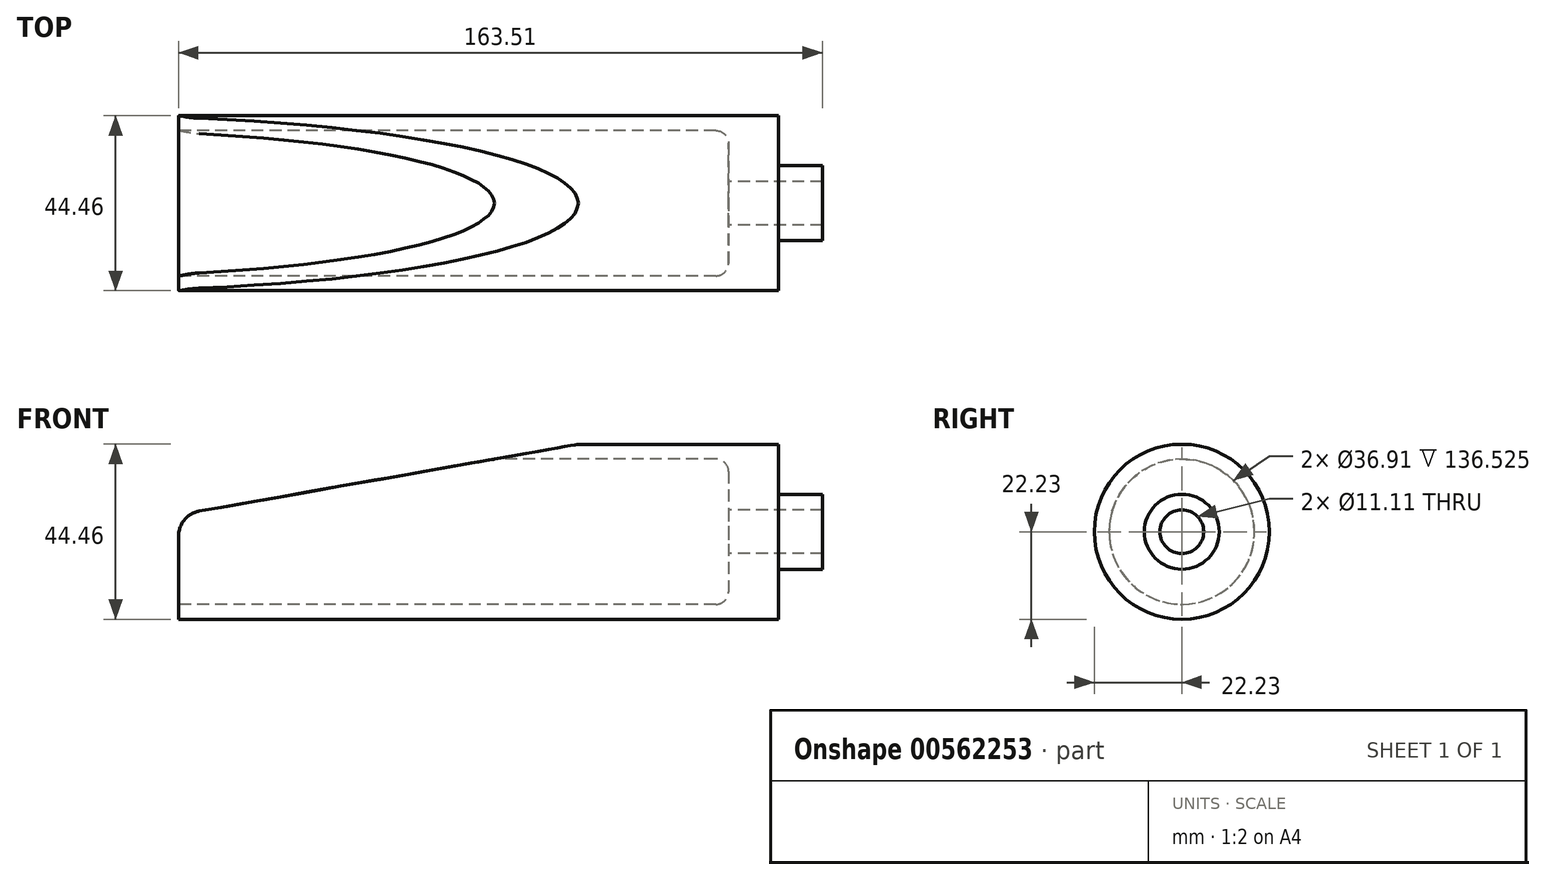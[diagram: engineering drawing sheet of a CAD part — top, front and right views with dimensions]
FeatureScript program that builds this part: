
annotation { "Feature Type Name" : "Feature", "Feature Type Description" : "" }
export const myFeature = defineFeature(function(context is Context, id is Id, definition is map)
    precondition{}
    {
        {
            var Q0;
            Q0=qCreatedBy(makeId("Front.planeOp"),FACE);
            var sketch = newSketch(context, id + "F0", { "sketchPlane" : qUnion([Q0])});
            skLineSegment(sketch, "E0", {"start": v(-163.51, 0) * mm, "end": v(0, 0) * mm, "construction": true});
            skLineSegment(sketch, "E1", {"start": v(0, 0) * mm, "end": v(0, 0) * mm});
            skLineSegment(sketch, "E2", {"start": v(0, -9.53) * mm, "end": v(-11.11, -9.53) * mm});
            skLineSegment(sketch, "E3", {"start": v(-11.11, -9.53) * mm, "end": v(-11.11, -22.23) * mm});
            skLineSegment(sketch, "E4", {"start": v(-11.11, -22.23) * mm, "end": v(-163.51, -22.23) * mm});
            skLineSegment(sketch, "E5", {"start": v(-163.51, -22.23) * mm, "end": v(-163.51, -18.46) * mm});
            skLineSegment(sketch, "E6", {"start": v(-163.51, -18.46) * mm, "end": v(-26.99, -18.46) * mm});
            skLineSegment(sketch, "E7", {"start": v(-23.81, -15.28) * mm, "end": v(-23.81, -5.56) * mm});
            skLineSegment(sketch, "E8", {"start": v(-23.81, 0) * mm, "end": v(0, 0) * mm, "construction": true});
            skLineSegment(sketch, "E9", {"start": v(0, 0) * mm, "end": v(0, -5.56) * mm, "construction": true});
            skPoint(sketch, "E10.visualSharp", {"position": v(-23.81, -18.46) * mm});
            skArc(sketch, "E10.filletArc", {"start": v(-26.99, -18.46) * mm, "mid": v(-24.74, -17.53) * mm, "end": v(-23.81, -15.28) * mm});
            skLineSegment(sketch, "E11", {"start": v(-23.81, -5.56) * mm, "end": v(0, -5.56) * mm});
            skLineSegment(sketch, "E12", {"start": v(-23.81, -5.56) * mm, "end": v(-23.81, 0) * mm, "construction": true});
            skLineSegment(sketch, "E13", {"start": v(0, -5.56) * mm, "end": v(0, -5.56) * mm});
            skLineSegment(sketch, "E14", {"start": v(0, -5.56) * mm, "end": v(0, -9.53) * mm});
            skSolve(sketch);
        }
        {
            var Q0;
            Q0=qSketchRegion(id+"F0",true);
            var Q1;
            Q1=sQuery(id+"F0.wireOp",EDGE,"E0");
            revolve(context, id + "F1", {"entities" : qUnion([Q0]), "axis" : qUnion([Q1]), "revolveType" : RevolveType.FULL});
        }
        {
            var Q0;
            Q0=qCreatedBy(makeId("Front.planeOp"),FACE);
            var sketch = newSketch(context, id + "F2", { "sketchPlane" : qUnion([Q0])});
            skLineSegment(sketch, "E15", {"start": v(-169.86, 22.22) * mm, "end": v(-61.91, 22.22) * mm});
            skLineSegment(sketch, "E16", {"start": v(-61.91, 22.22) * mm, "end": v(-158.27, 5.24) * mm});
            skLineSegment(sketch, "E17", {"start": v(-163.51, -1.02) * mm, "end": v(-163.51, -22.22) * mm});
            skLineSegment(sketch, "E18", {"start": v(-163.51, -22.22) * mm, "end": v(-169.86, -22.22) * mm});
            skLineSegment(sketch, "E19", {"start": v(-169.86, -22.22) * mm, "end": v(-169.86, 22.22) * mm});
            skPoint(sketch, "E20.visualSharp", {"position": v(-163.51, 4.31) * mm});
            skArc(sketch, "E20.filletArc", {"start": v(-158.27, 5.24) * mm, "mid": v(-162.03, 3.06) * mm, "end": v(-163.51, -1.02) * mm});
            skLineSegment(sketch, "E21", {"start": v(-169.86, 0) * mm, "end": v(0, 0) * mm, "construction": true});
            skSolve(sketch);
        }
        {
            var Q0;
            Q0=qSketchRegion(id+"F2",true);
            extrude(context, id + "F3", {"entities" : qUnion([Q0]), "operationType" : NewBodyOperationType.REMOVE, "oppositeDirection" : true, "depth" : 76.2 * mm, "offsetDistance" : 25.4 * mm, "symmetric" : true});
        }
    });
